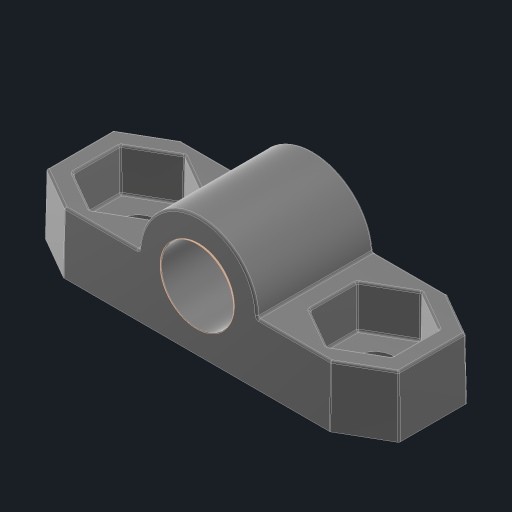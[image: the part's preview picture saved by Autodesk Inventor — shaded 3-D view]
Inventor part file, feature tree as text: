
AUTODESK INVENTOR PART (.ipt)
format: ipt  version: 2023 (Build 270158030, 158C)  size: 811,520 bytes
history: native  units: in
note: dims shown in document units (in); Inventor stores cm internally (conversion verified against a paired STEP export)
features: sketch x1, other x1, fillet x1, extrude x1
ambient origin geometry x8: Origin, YZ Plane, XZ Plane, XY Plane, X Axis, Y Axis, Z Axis, Center Point
bodies: Solid1 (feature_tree)
feature tree (4):
  sketch  "Sketch3"  dims[d3=0.5in d4=0.0in]
  other  "Srf1"
  fillet  "Fillet7"  Radius=0.311in
  extrude  "ExtrusionSrf1"  [1 undecoded]
note: 1 required parameter value undecoded (feature->parameter linkage not recoverable at this tier; creation-order binding heuristic only, values carry confidence <= 0.55)
